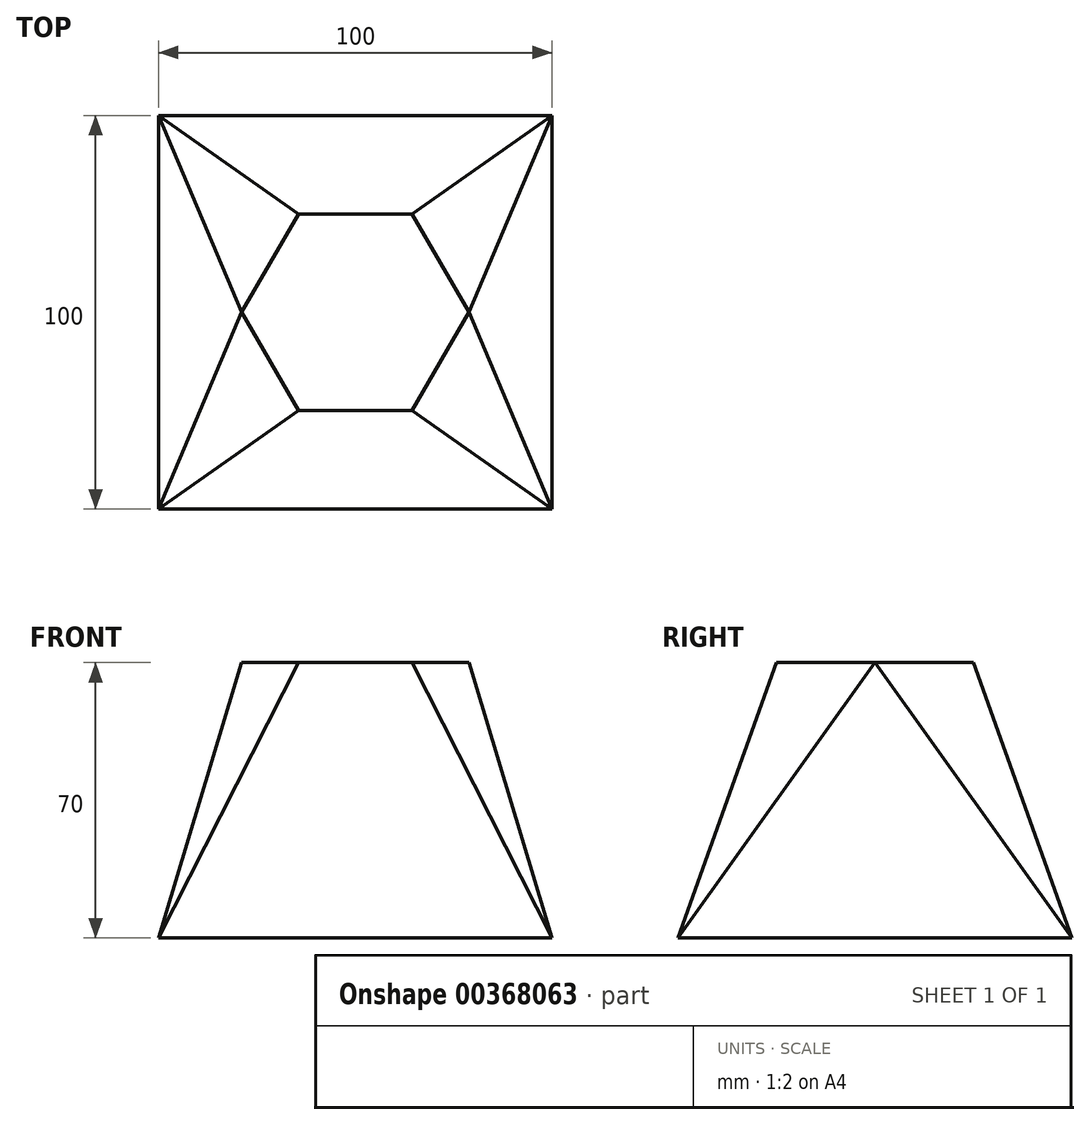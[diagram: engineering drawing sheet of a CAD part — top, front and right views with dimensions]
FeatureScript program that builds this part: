
annotation { "Feature Type Name" : "Feature", "Feature Type Description" : "" }
export const myFeature = defineFeature(function(context is Context, id is Id, definition is map)
    precondition{}
    {
        {
            var Q0;
            Q0=qCreatedBy(makeId("Top.planeOp"),FACE);
            var sketch = newSketch(context, id + "F0", { "sketchPlane" : qUnion([Q0])});
            skLineSegment(sketch, "E0.bottom", {"start": v(-50, -50) * mm, "end": v(50, -50) * mm});
            skLineSegment(sketch, "E0.top", {"start": v(-50, 50) * mm, "end": v(50, 50) * mm});
            skLineSegment(sketch, "E0.left", {"start": v(-50, -50) * mm, "end": v(-50, 50) * mm});
            skLineSegment(sketch, "E0.right", {"start": v(50, -50) * mm, "end": v(50, 50) * mm});
            skPoint(sketch, "E0.middle", {"position": v(0, 0) * mm});
            skSolve(sketch);
        }
        {
            var Q0;
            Q0=qCreatedBy(makeId("Top.planeOp"),FACE);
            cPlane(context, id + "F1", {"entities" : qUnion([Q0]), "cplaneType" : CPlaneType.OFFSET, "offset" : 70 * mm, "width" : 150 * mm, "height" : 150 * mm});
        }
        {
            var Q0;
            Q0=qCreatedBy(id+"F1.planeOp",FACE);
            var sketch = newSketch(context, id + "F2", { "sketchPlane" : qUnion([Q0])});
            skCircle(sketch, "E1.cCircle", {"center": v(0, 0) * mm, "radius": 25 * mm, "construction": true});
            skLineSegment(sketch, "E1.0", {"start": v(-14.43, 25) * mm, "end": v(14.43, 25) * mm});
            skLineSegment(sketch, "E1.1", {"start": v(14.43, 25) * mm, "end": v(28.87, 0) * mm});
            skLineSegment(sketch, "E1.2", {"start": v(28.87, 0) * mm, "end": v(14.43, -25) * mm});
            skLineSegment(sketch, "E1.3", {"start": v(14.43, -25) * mm, "end": v(-14.43, -25) * mm});
            skLineSegment(sketch, "E1.4", {"start": v(-14.43, -25) * mm, "end": v(-28.87, 0) * mm});
            skLineSegment(sketch, "E1.5", {"start": v(-28.87, 0) * mm, "end": v(-14.43, 25) * mm});
            skPoint(sketch, "E1.0.midPoint", {"position": v(0, 25) * mm});
            skLineSegment(sketch, "E2", {"start": v(-14.43, 25) * mm, "end": v(-14.43, -25) * mm});
            skLineSegment(sketch, "E3", {"start": v(14.43, -25) * mm, "end": v(14.43, 25) * mm});
            skSolve(sketch);
        }
        {
            var Q0;
            Q0=makeQuery(id+"F0.imprint","IMPRINT",FACE,{"disambiguationData":[TD([[makeQuery(id+"F0.imprint","IMPRINT",EDGE,{"derivedFrom":sQuery(id+"F0.wireOp",EDGE,"E0.bottom")}),1.0]])]});
            var Q1;
            Q1=makeQuery(id+"F2.imprint","IMPRINT",FACE,{"disambiguationData":[TD([[makeQuery(id+"F2.imprint","IMPRINT",EDGE,{"derivedFrom":sQuery(id+"F2.wireOp",EDGE,"E1.0")}),-1.0]])]});
            loft(context, id + "F3", {"sheetProfilesArray" : [{ "sheetProfileEntities" : qUnion([Q0]) }, { "sheetProfileEntities" : qUnion([Q1]) }]});
        }
        {
            var Q1;
            Q1=makeQuery(id+"F2.imprint","IMPRINT",FACE,{"disambiguationData":[TD([[makeQuery(id+"F2.imprint","IMPRINT",EDGE,{"derivedFrom":sQuery(id+"F2.wireOp",EDGE,"E1.4")}),-1.0]])]});
            var Q2;
            Q2=sQuery(id+"F0.wireOp",VERTEX,"E0.left.end");
            loft(context, id + "F4", {"operationType" : NewBodyOperationType.ADD, "sheetProfilesArray" : [{ "sheetProfileEntities" : qUnion([Q1]) }, { "sheetProfileEntities" : qUnion([Q2]) }]});
        }
        {
            var Q1;
            Q1=makeQuery(id+"F2.imprint","IMPRINT",FACE,{"disambiguationData":[TD([[makeQuery(id+"F2.imprint","IMPRINT",EDGE,{"derivedFrom":sQuery(id+"F2.wireOp",EDGE,"E1.4")}),-1.0]])]});
            var Q2;
            Q2=sQuery(id+"F0.wireOp",VERTEX,"E0.left.start");
            loft(context, id + "F5", {"operationType" : NewBodyOperationType.ADD, "sheetProfilesArray" : [{ "sheetProfileEntities" : qUnion([Q1]) }, { "sheetProfileEntities" : qUnion([Q2]) }]});
        }
        {
            var Q1;
            Q1=makeQuery(id+"F4.opLoft","SWEPT_FACE",FACE,{"disambiguationData":[OSD([sQuery(id+"F2.wireOp",EDGE,"E1.3"),sQuery(id+"F2.wireOp",EDGE,"E1.4"),sQuery(id+"F2.wireOp",EDGE,"E1.5"),sQuery(id+"F2.wireOp",EDGE,"E2")])]});
            var Q2;
            Q2=makeQuery(id+"F5.opLoft","SWEPT_FACE",FACE,{"disambiguationData":[OSD([sQuery(id+"F2.wireOp",EDGE,"E1.0"),sQuery(id+"F2.wireOp",EDGE,"E1.4"),sQuery(id+"F2.wireOp",EDGE,"E1.5"),sQuery(id+"F2.wireOp",EDGE,"E2")])]});
            var Q3;
            Q3=sQuery(id+"F0.wireOp",VERTEX,"E0.left.end");
            var Q4;
            Q4=sQuery(id+"F0.wireOp",VERTEX,"E0.left.start");
            loft(context, id + "F6", {"operationType" : NewBodyOperationType.ADD, "sheetProfilesArray" : [{ "sheetProfileEntities" : qUnion([Q1]) }, { "sheetProfileEntities" : qUnion([Q2]) }], "matchConnections" : true, "connections" : [{ "connectionEntities" : qUnion([Q3, Q4]), "connectionEdgeQueries" : qUnion([]), "connectionEdgeParameters" : [] }]});
        }
        {
            var Q1;
            Q1=makeQuery(id+"F2.imprint","IMPRINT",FACE,{"disambiguationData":[TD([[makeQuery(id+"F2.imprint","IMPRINT",EDGE,{"derivedFrom":sQuery(id+"F2.wireOp",EDGE,"E1.1")}),-1.0]])]});
            var Q2;
            Q2=sQuery(id+"F0.wireOp",VERTEX,"E0.right.start");
            loft(context, id + "F7", {"operationType" : NewBodyOperationType.ADD, "sheetProfilesArray" : [{ "sheetProfileEntities" : qUnion([Q1]) }, { "sheetProfileEntities" : qUnion([Q2]) }]});
        }
        {
            var Q1;
            Q1=makeQuery(id+"F2.imprint","IMPRINT",FACE,{"disambiguationData":[TD([[makeQuery(id+"F2.imprint","IMPRINT",EDGE,{"derivedFrom":sQuery(id+"F2.wireOp",EDGE,"E1.1")}),-1.0]])]});
            var Q2;
            Q2=sQuery(id+"F0.wireOp",VERTEX,"E0.right.end");
            loft(context, id + "F8", {"operationType" : NewBodyOperationType.ADD, "sheetProfilesArray" : [{ "sheetProfileEntities" : qUnion([Q1]) }, { "sheetProfileEntities" : qUnion([Q2]) }]});
        }
        {
            var Q1;
            Q1=makeQuery(id+"F8.opLoft","SWEPT_FACE",FACE,{"disambiguationData":[OSD([sQuery(id+"F2.wireOp",EDGE,"E1.1"),sQuery(id+"F2.wireOp",EDGE,"E1.2"),sQuery(id+"F2.wireOp",EDGE,"E1.3"),sQuery(id+"F2.wireOp",EDGE,"E3")])]});
            var Q2;
            Q2=makeQuery(id+"F7.opLoft","SWEPT_FACE",FACE,{"disambiguationData":[OSD([sQuery(id+"F2.wireOp",EDGE,"E1.0"),sQuery(id+"F2.wireOp",EDGE,"E1.1"),sQuery(id+"F2.wireOp",EDGE,"E1.2"),sQuery(id+"F2.wireOp",EDGE,"E3")])]});
            var Q3;
            Q3=sQuery(id+"F0.wireOp",VERTEX,"E0.right.start");
            var Q4;
            Q4=sQuery(id+"F0.wireOp",VERTEX,"E0.right.end");
            loft(context, id + "F9", {"operationType" : NewBodyOperationType.ADD, "sheetProfilesArray" : [{ "sheetProfileEntities" : qUnion([Q1]) }, { "sheetProfileEntities" : qUnion([Q2]) }], "matchConnections" : true, "connections" : [{ "connectionEntities" : qUnion([Q3, Q4]), "connectionEdgeQueries" : qUnion([]), "connectionEdgeParameters" : [] }]});
        }
    });
